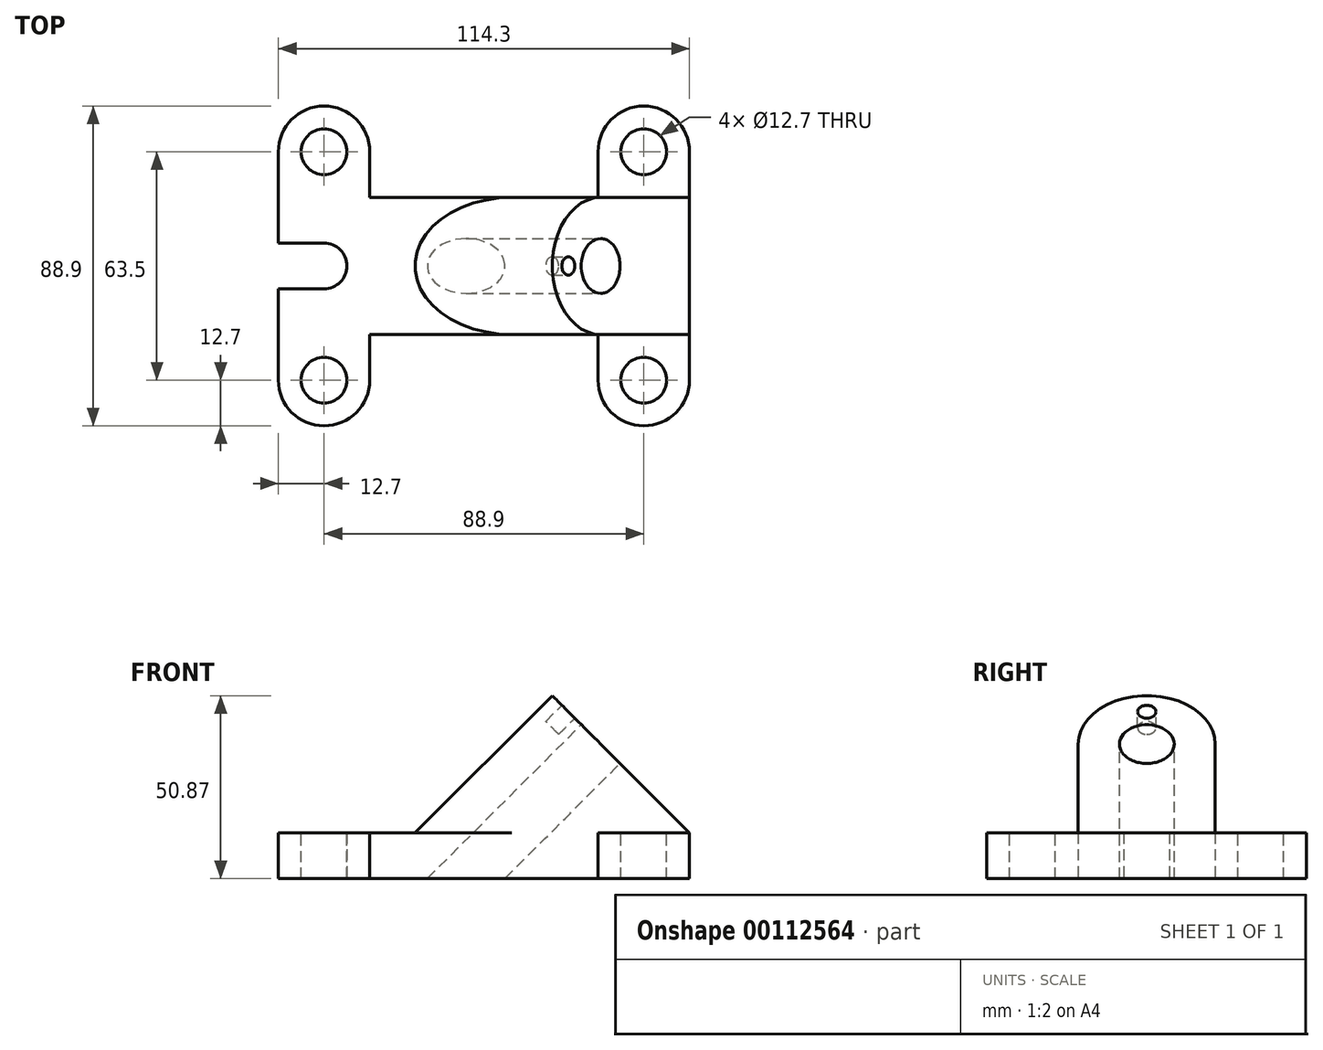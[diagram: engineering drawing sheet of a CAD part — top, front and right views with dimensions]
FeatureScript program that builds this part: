
annotation { "Feature Type Name" : "Feature", "Feature Type Description" : "" }
export const myFeature = defineFeature(function(context is Context, id is Id, definition is map)
    precondition{}
    {
        {
            var Q0;
            Q0=qCreatedBy(makeId("Top.planeOp"),FACE);
            var sketch = newSketch(context, id + "F0", { "sketchPlane" : qUnion([Q0])});
            skLineSegment(sketch, "E0", {"start": v(0, 0) * mm, "end": v(63.5, 0) * mm});
            skLineSegment(sketch, "E1", {"start": v(63.5, 0) * mm, "end": v(63.5, 12.7) * mm});
            skArc(sketch, "E2", {"start": v(88.9, 12.7) * mm, "mid": v(76.2, 25.4) * mm, "end": v(63.5, 12.7) * mm});
            skLineSegment(sketch, "E3", {"start": v(88.9, 12.7) * mm, "end": v(88.9, -50.8) * mm});
            skArc(sketch, "E4", {"start": v(63.5, -50.8) * mm, "mid": v(76.2, -63.5) * mm, "end": v(88.9, -50.8) * mm});
            skLineSegment(sketch, "E5", {"start": v(63.5, -50.8) * mm, "end": v(63.5, -38.1) * mm});
            skLineSegment(sketch, "E6", {"start": v(63.5, -38.1) * mm, "end": v(0, -38.1) * mm});
            skLineSegment(sketch, "E7", {"start": v(0, -38.1) * mm, "end": v(0, -50.8) * mm});
            skArc(sketch, "E8", {"start": v(-25.4, -50.8) * mm, "mid": v(-12.7, -63.5) * mm, "end": v(0, -50.8) * mm});
            skLineSegment(sketch, "E9", {"start": v(-25.4, -50.8) * mm, "end": v(-25.4, -25.4) * mm});
            skLineSegment(sketch, "E10", {"start": v(-25.4, -25.4) * mm, "end": v(-12.7, -25.4) * mm});
            skArc(sketch, "E11", {"start": v(-12.7, -25.4) * mm, "mid": v(-6.35, -19.05) * mm, "end": v(-12.7, -12.7) * mm});
            skLineSegment(sketch, "E12", {"start": v(-12.7, -12.7) * mm, "end": v(-25.4, -12.7) * mm});
            skLineSegment(sketch, "E13", {"start": v(-25.4, -12.7) * mm, "end": v(-25.4, 12.7) * mm});
            skArc(sketch, "E14", {"start": v(0, 12.7) * mm, "mid": v(-12.7, 25.4) * mm, "end": v(-25.4, 12.7) * mm});
            skLineSegment(sketch, "E15", {"start": v(0, 12.7) * mm, "end": v(0, 0) * mm});
            skSolve(sketch);
        }
        {
            var Q0;
            Q0=makeQuery(id+"F0.imprint","IMPRINT",FACE,{"disambiguationData":[TD([[makeQuery(id+"F0.imprint","IMPRINT",EDGE,{"derivedFrom":sQuery(id+"F0.wireOp",EDGE,"E0")}),-1.0]])]});
            extrude(context, id + "F1", {"entities" : qUnion([Q0]), "depth" : 12.7 * mm});
        }
        {
            var Q0;
            Q0=makeQuery(id+"F1.opExtrude","CAP_FACE",FACE,{"disambiguationData":[OSD([sQuery(id+"F0.wireOp",EDGE,"E0"),sQuery(id+"F0.wireOp",EDGE,"E1"),sQuery(id+"F0.wireOp",EDGE,"E2"),sQuery(id+"F0.wireOp",EDGE,"E3"),sQuery(id+"F0.wireOp",EDGE,"E4"),sQuery(id+"F0.wireOp",EDGE,"E5"),sQuery(id+"F0.wireOp",EDGE,"E6"),sQuery(id+"F0.wireOp",EDGE,"E7"),sQuery(id+"F0.wireOp",EDGE,"E8"),sQuery(id+"F0.wireOp",EDGE,"E9"),sQuery(id+"F0.wireOp",EDGE,"E10"),sQuery(id+"F0.wireOp",EDGE,"E11"),sQuery(id+"F0.wireOp",EDGE,"E12"),sQuery(id+"F0.wireOp",EDGE,"E13"),sQuery(id+"F0.wireOp",EDGE,"E14"),sQuery(id+"F0.wireOp",EDGE,"E15")])],"isStart":false});
            var sketch = newSketch(context, id + "F2", { "sketchPlane" : qUnion([Q0])});
            skCircle(sketch, "E16", {"center": v(-12.7, 12.7) * mm, "radius": 6.35 * mm});
            skCircle(sketch, "E17", {"center": v(76.2, 12.7) * mm, "radius": 6.35 * mm});
            skCircle(sketch, "E18", {"center": v(76.2, -50.8) * mm, "radius": 6.35 * mm});
            skCircle(sketch, "E19", {"center": v(-12.7, -50.8) * mm, "radius": 6.35 * mm});
            skSolve(sketch);
        }
        {
            var Q0;
            Q0=makeQuery(id+"F2.imprint","IMPRINT",FACE,{"disambiguationData":[TD([[makeQuery(id+"F2.imprint","IMPRINT",EDGE,{"derivedFrom":sQuery(id+"F2.wireOp",EDGE,"E16")}),1.0]])]});
            var Q1;
            Q1=makeQuery(id+"F2.imprint","IMPRINT",FACE,{"disambiguationData":[TD([[makeQuery(id+"F2.imprint","IMPRINT",EDGE,{"derivedFrom":sQuery(id+"F2.wireOp",EDGE,"E17")}),1.0]])]});
            var Q2;
            Q2=makeQuery(id+"F2.imprint","IMPRINT",FACE,{"disambiguationData":[TD([[makeQuery(id+"F2.imprint","IMPRINT",EDGE,{"derivedFrom":sQuery(id+"F2.wireOp",EDGE,"E18")}),1.0]])]});
            var Q3;
            Q3=makeQuery(id+"F2.imprint","IMPRINT",FACE,{"disambiguationData":[TD([[makeQuery(id+"F2.imprint","IMPRINT",EDGE,{"derivedFrom":sQuery(id+"F2.wireOp",EDGE,"E19")}),1.0]])]});
            extrude(context, id + "F3", {"entities" : qUnion([Q0, Q1, Q2, Q3]), "operationType" : NewBodyOperationType.REMOVE, "endBound" : BoundingType.THROUGH_ALL, "oppositeDirection" : true, "depth" : 25.4 * mm});
        }
        {
            var Q0;
            Q0=qCreatedBy(makeId("Front.planeOp"),FACE);
            var sketch = newSketch(context, id + "F4", { "sketchPlane" : qUnion([Q0])});
            skLineSegment(sketch, "E20", {"start": v(88.9, 0) * mm, "end": v(38.09, 0) * mm, "construction": true});
            skLineSegment(sketch, "E21", {"start": v(88.9, 0) * mm, "end": v(88.9, 12.7) * mm, "construction": true});
            skLineSegment(sketch, "E22", {"start": v(88.9, 12.7) * mm, "end": v(53.6, 48) * mm, "construction": true});
            skSolve(sketch);
        }
        {
            var Q0;
            Q0=makeQuery(id+"F1.opExtrude","CAP_EDGE",EDGE,{"disambiguationData":[OSD([sQuery(id+"F0.wireOp",EDGE,"E3")])],"isStart":false});
            var Q1;
            Q1=makeQuery(id+"F2.imprint","IMPRINT",FACE,{"disambiguationData":[TD([[makeQuery(id+"F2.imprint","IMPRINT",EDGE,{"derivedFrom":sQuery(id+"F2.wireOp",EDGE,"E16")}),-1.0]])]});
            cPlane(context, id + "F5", {"entities" : qUnion([Q0, Q1]), "cplaneType" : CPlaneType.LINE_ANGLE, "offset" : 25.4 * mm, "angle" : 135 * degree, "width" : 152.4 * mm, "height" : 152.4 * mm});
        }
        {
            var Q0;
            Q0=qCreatedBy(id+"F5.planeOp",FACE);
            var sketch = newSketch(context, id + "F6", { "sketchPlane" : qUnion([Q0])});
            skLineSegment(sketch, "E23", {"start": v(-38.1, -53.88) * mm, "end": v(0, -53.88) * mm});
            skLineSegment(sketch, "E24", {"start": v(0, -53.88) * mm, "end": v(0, -18.96) * mm});
            skArc(sketch, "E25", {"start": v(0, -18.96) * mm, "mid": v(-19.05, 0.1) * mm, "end": v(-38.1, -18.96) * mm});
            skLineSegment(sketch, "E26", {"start": v(-38.1, -18.96) * mm, "end": v(-38.1, -53.88) * mm});
            skSolve(sketch);
        }
        {
            var Q0;
            Q0=makeQuery(id+"F6.imprint","IMPRINT",FACE,{"disambiguationData":[TD([[makeQuery(id+"F6.imprint","IMPRINT",EDGE,{"derivedFrom":sQuery(id+"F6.wireOp",EDGE,"E23")}),1.0]])]});
            extrude(context, id + "F7", {"entities" : qUnion([Q0]), "operationType" : NewBodyOperationType.ADD, "endBound" : BoundingType.UP_TO_NEXT, "oppositeDirection" : true, "depth" : 25.4 * mm});
        }
        {
            var Q0;
            Q0=qCreatedBy(id+"F5.planeOp",FACE);
            var sketch = newSketch(context, id + "F8", { "sketchPlane" : qUnion([Q0])});
            skCircle(sketch, "E27", {"center": v(-19.05, -18.96) * mm, "radius": 7.62 * mm});
            skSolve(sketch);
        }
        {
            var Q0;
            Q0=makeQuery(id+"F8.imprint","IMPRINT",FACE,{"disambiguationData":[TD([[makeQuery(id+"F8.imprint","IMPRINT",EDGE,{"derivedFrom":sQuery(id+"F8.wireOp",EDGE,"E27")}),1.0]])]});
            extrude(context, id + "F9", {"entities" : qUnion([Q0]), "operationType" : NewBodyOperationType.REMOVE, "endBound" : BoundingType.THROUGH_ALL, "oppositeDirection" : true, "depth" : 25.4 * mm});
        }
        {
            var Q0;
            Q0=qCreatedBy(id+"F5.planeOp",FACE);
            var sketch = newSketch(context, id + "F10", { "sketchPlane" : qUnion([Q0])});
            skCircle(sketch, "E28", {"center": v(-19.05, -6.26) * mm, "radius": 2.54 * mm});
            skSolve(sketch);
        }
        {
            var Q0;
            Q0 = qSketchRegion(id + "F10", true);
            extrude(context, id + "F11", {"entities" : qUnion([Q0]), "operationType" : NewBodyOperationType.REMOVE, "oppositeDirection" : true, "depth" : 6.35 * mm});
        }
    });
